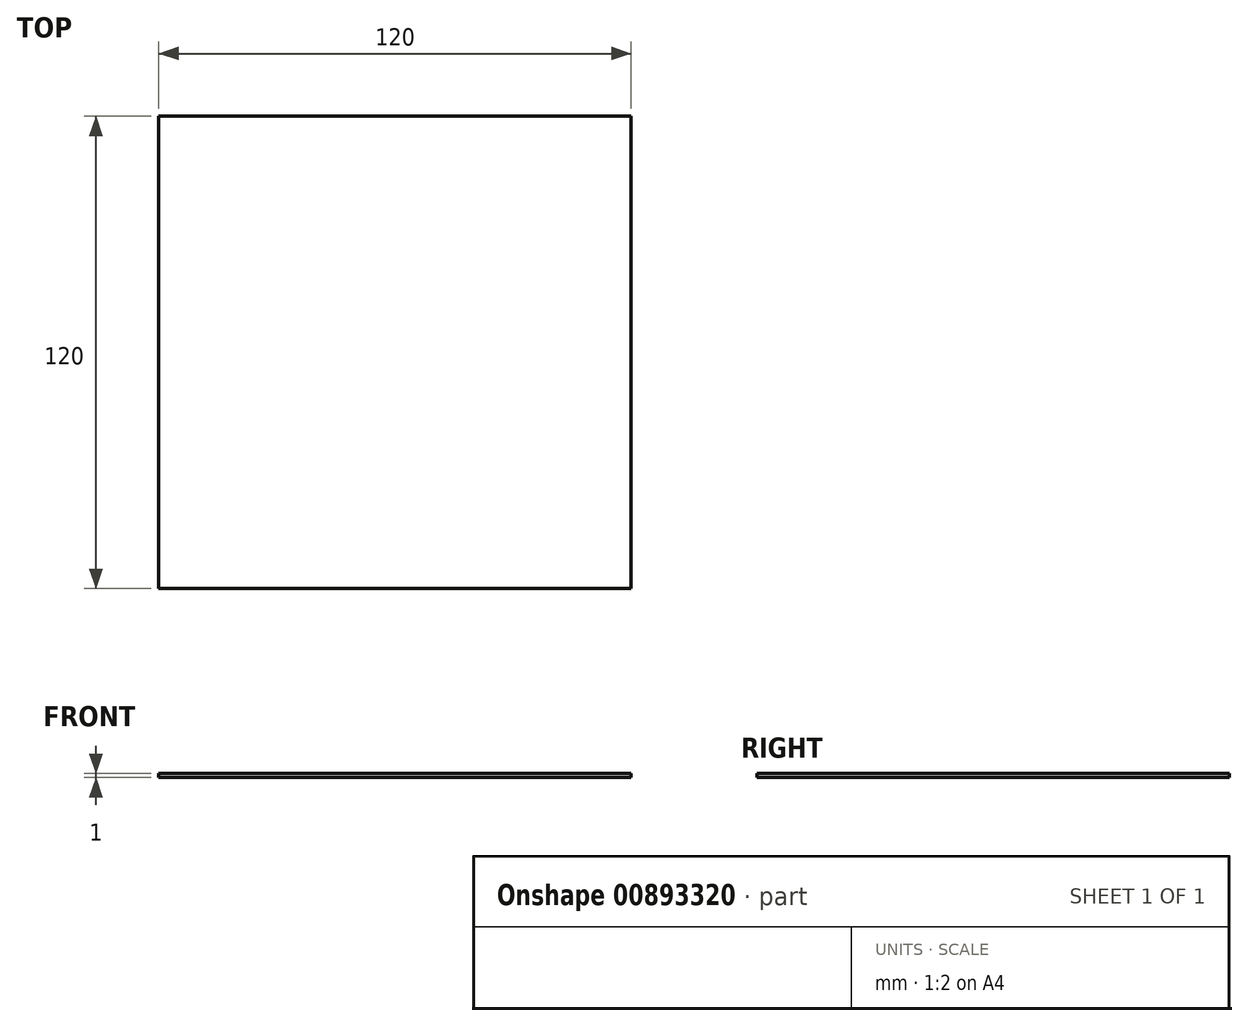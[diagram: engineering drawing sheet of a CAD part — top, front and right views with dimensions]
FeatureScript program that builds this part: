
annotation { "Feature Type Name" : "Feature", "Feature Type Description" : "" }
export const myFeature = defineFeature(function(context is Context, id is Id, definition is map)
    precondition{}
    {
        {
            var Q0;
            Q0=qCreatedBy(makeId("Top.planeOp"),FACE);
            var sketch = newSketch(context, id + "F0", { "sketchPlane" : qUnion([Q0])});
            skLineSegment(sketch, "E0.bottom", {"start": v(-60, 60) * mm, "end": v(60, 60) * mm});
            skLineSegment(sketch, "E0.top", {"start": v(-60, -60) * mm, "end": v(60, -60) * mm});
            skLineSegment(sketch, "E0.left", {"start": v(-60, 60) * mm, "end": v(-60, -60) * mm});
            skLineSegment(sketch, "E0.right", {"start": v(60, 60) * mm, "end": v(60, -60) * mm});
            skPoint(sketch, "E0.middle", {"position": v(0, 0) * mm});
            skSolve(sketch);
        }
        {
            var Q0;
            Q0=makeQuery(id+"F0.imprint","IMPRINT",FACE,{"disambiguationData":[TD([[makeQuery(id+"F0.imprint","IMPRINT",EDGE,{"derivedFrom":sQuery(id+"F0.wireOp",EDGE,"E0.bottom")}),-1.0]])]});
            extrude(context, id + "F1", {"entities" : qUnion([Q0]), "oppositeDirection" : true, "depth" : 1 * mm, "offsetDistance" : 25 * mm});
        }
    });
